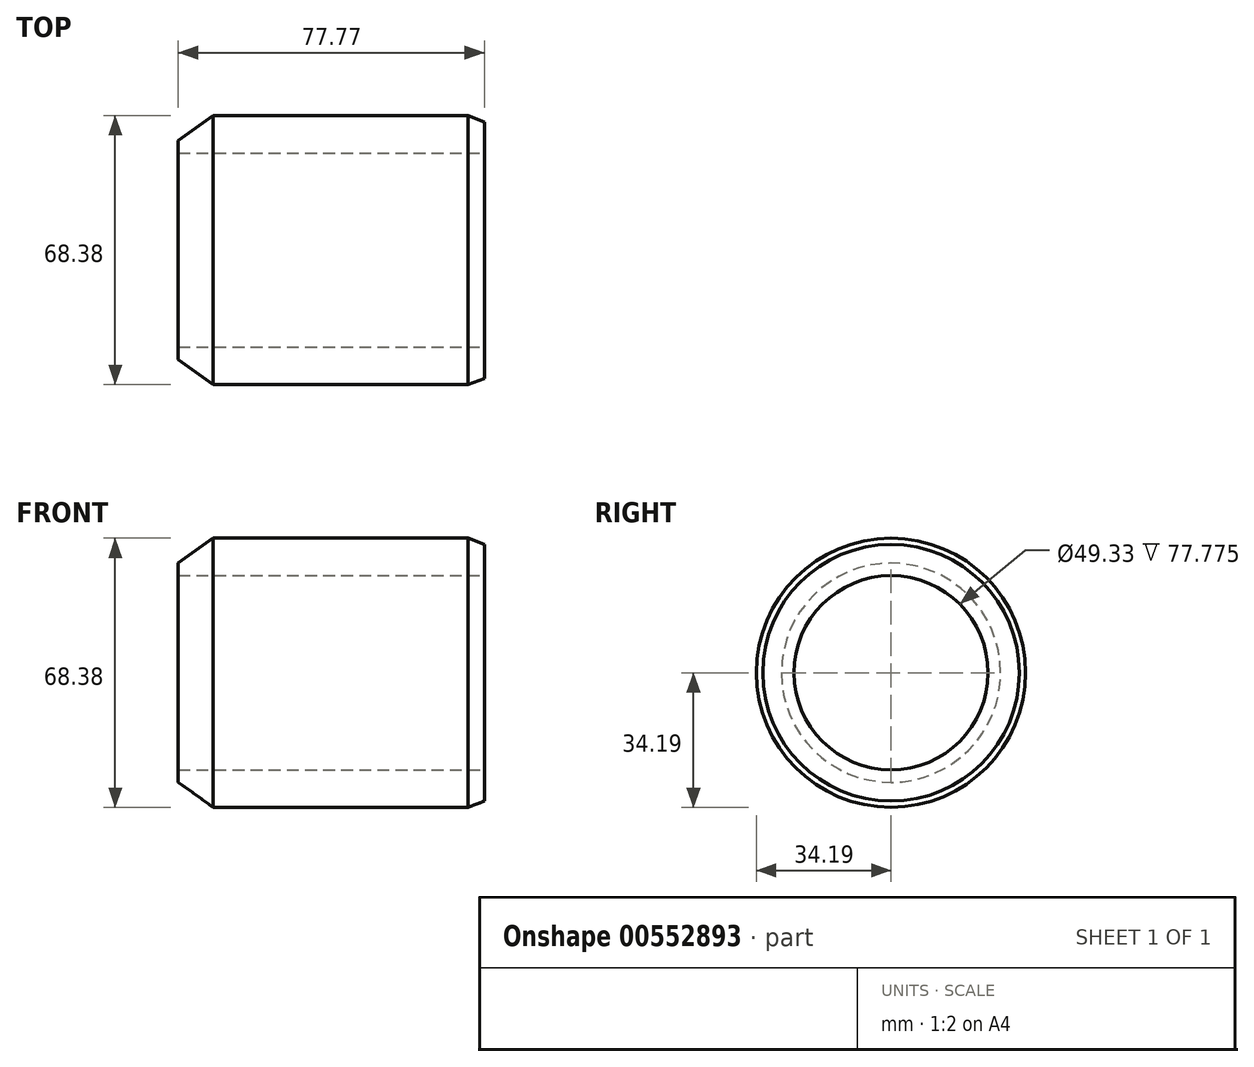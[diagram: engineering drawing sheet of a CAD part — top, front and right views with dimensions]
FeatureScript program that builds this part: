
annotation { "Feature Type Name" : "Feature", "Feature Type Description" : "" }
export const myFeature = defineFeature(function(context is Context, id is Id, definition is map)
    precondition{}
    {
        {
            var Q0;
            Q0=qCreatedBy(makeId("Top.planeOp"),FACE);
            var sketch = newSketch(context, id + "F0", { "sketchPlane" : qUnion([Q0])});
            skLineSegment(sketch, "E0.bottom", {"start": v(-68.9, 34.19) * mm, "end": v(-4.13, 34.19) * mm});
            skLineSegment(sketch, "E0.top", {"start": v(-77.77, 24.66) * mm, "end": v(0, 24.66) * mm});
            skLineSegment(sketch, "E0.left", {"start": v(-77.77, 27.84) * mm, "end": v(-77.77, 24.66) * mm});
            skLineSegment(sketch, "E0.right", {"start": v(0, 32.58) * mm, "end": v(0, 24.66) * mm});
            skLineSegment(sketch, "E1", {"start": v(0, 0) * mm, "end": v(-171.47, 0) * mm, "construction": true});
            skPoint(sketch, "E2.visualSharp", {"position": v(-77.77, 34.19) * mm});
            skLineSegment(sketch, "E3", {"start": v(-77.77, 27.84) * mm, "end": v(-68.9, 34.19) * mm});
            skPoint(sketch, "E4.visualSharp", {"position": v(0, 34.19) * mm});
            skLineSegment(sketch, "E5", {"start": v(-4.13, 34.19) * mm, "end": v(0, 32.58) * mm});
            skSolve(sketch);
        }
        {
            var Q0;
            Q0 = qSketchRegion(id + "F0", true);
            var Q1;
            Q1=sQuery(id+"F0.wireOp",EDGE,"E1");
            revolve(context, id + "F1", {"entities" : qUnion([Q0]), "axis" : qUnion([Q1]), "revolveType" : RevolveType.FULL});
        }
    });
